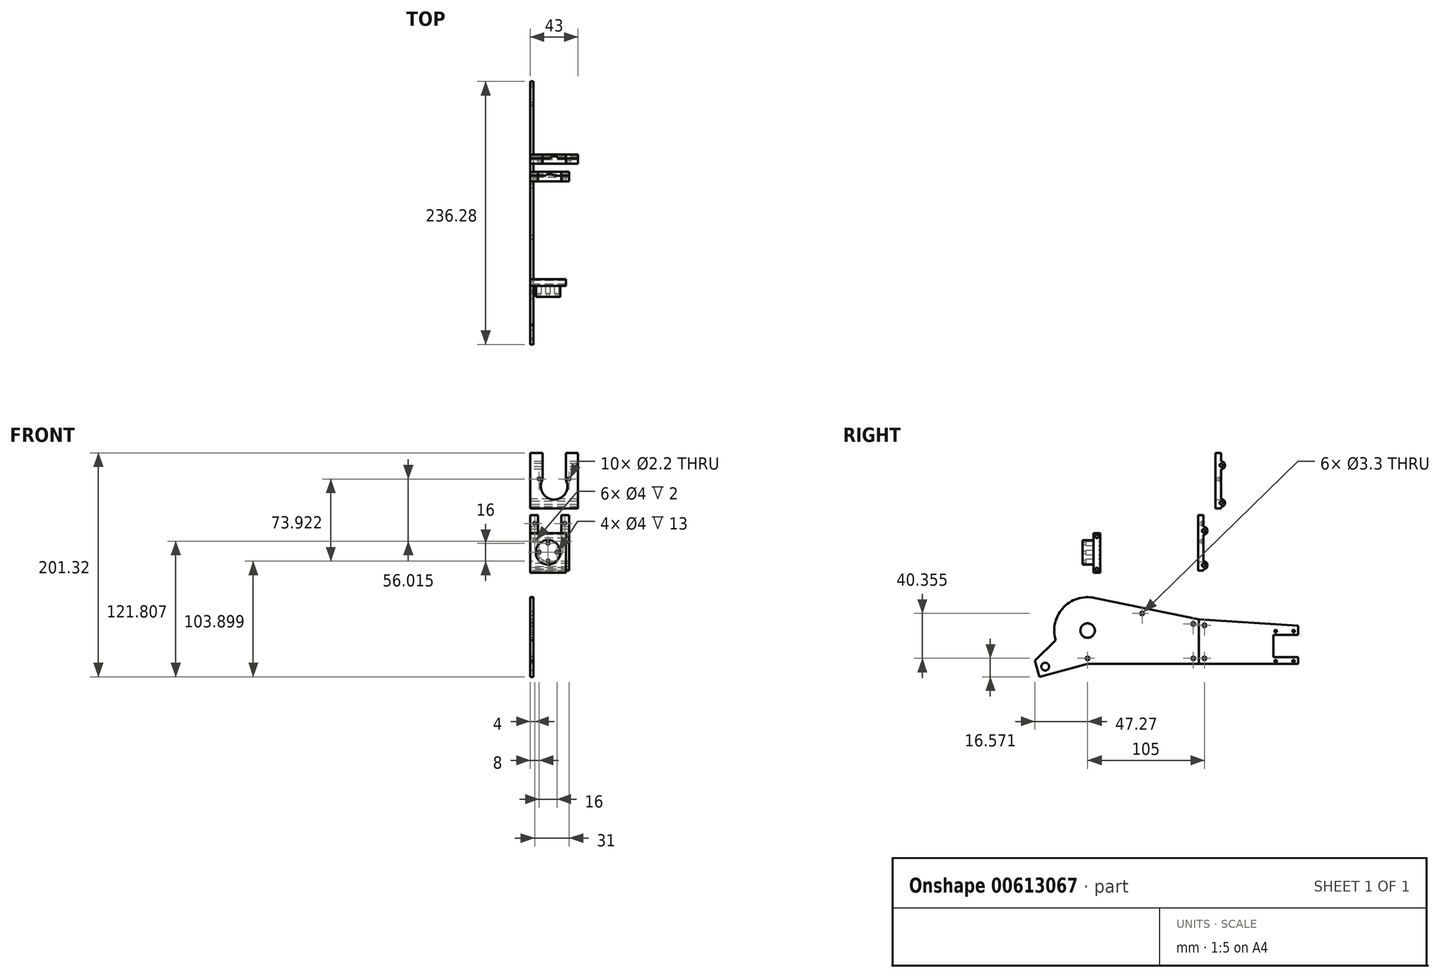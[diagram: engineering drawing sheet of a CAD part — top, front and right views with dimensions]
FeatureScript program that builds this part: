
annotation { "Feature Type Name" : "Feature", "Feature Type Description" : "" }
export const myFeature = defineFeature(function(context is Context, id is Id, definition is map)
    precondition{}
    {
        {
            var Q0;
            Q0=qCreatedBy(makeId("Right.planeOp"),FACE);
            var sketch = newSketch(context, id + "F0", { "sketchPlane" : qUnion([Q0])});
            skLineSegment(sketch, "E0", {"start": v(45.86, -61.42) * mm, "end": v(45.86, -101.42) * mm});
            skLineSegment(sketch, "E1", {"start": v(45.86, -101.42) * mm, "end": v(134.87, -101.42) * mm});
            skLineSegment(sketch, "E2", {"start": v(134.87, -101.42) * mm, "end": v(134.87, -95.42) * mm});
            skLineSegment(sketch, "E3", {"start": v(134.87, -66.9) * mm, "end": v(45.86, -61.42) * mm});
            skLineSegment(sketch, "E4", {"start": v(134.87, -95.42) * mm, "end": v(112.87, -95.42) * mm});
            skLineSegment(sketch, "E5", {"start": v(112.87, -95.42) * mm, "end": v(112.87, -75.42) * mm});
            skLineSegment(sketch, "E6", {"start": v(112.87, -75.42) * mm, "end": v(134.87, -75.42) * mm});
            skLineSegment(sketch, "E7.trimOffspring", {"start": v(134.87, -75.42) * mm, "end": v(134.87, -66.9) * mm});
            skPoint(sketch, "E8", {"position": v(50.86, -66.74) * mm});
            skPoint(sketch, "E9", {"position": v(50.86, -96.42) * mm});
            skCircle(sketch, "E10", {"center": v(145.37, -85.42) * mm, "radius": 11 * mm, "construction": true});
            skPoint(sketch, "E11", {"position": v(130.87, -98.92) * mm});
            skPoint(sketch, "E12", {"position": v(114.87, -98.92) * mm});
            skPoint(sketch, "E13", {"position": v(114.87, -71.92) * mm});
            skPoint(sketch, "E14", {"position": v(130.96, -71.92) * mm});
            skLineSegment(sketch, "E15", {"start": v(145.37, -85.42) * mm, "end": v(112.87, -85.42) * mm, "construction": true});
            skCircle(sketch, "E16", {"center": v(50.86, -66.74) * mm, "radius": 1.65 * mm});
            skCircle(sketch, "E17", {"center": v(50.86, -96.42) * mm, "radius": 1.65 * mm});
            skCircle(sketch, "E18", {"center": v(114.87, -71.92) * mm, "radius": 1.1 * mm});
            skCircle(sketch, "E19", {"center": v(130.96, -71.92) * mm, "radius": 1.1 * mm});
            skCircle(sketch, "E20", {"center": v(130.87, -98.92) * mm, "radius": 1.1 * mm});
            skCircle(sketch, "E21", {"center": v(114.87, -98.92) * mm, "radius": 1.1 * mm});
            skSolve(sketch);
        }
        {
            var Q0;
            Q0=makeQuery(id+"F0.imprint","IMPRINT",FACE,{"disambiguationData":[TD([[makeQuery(id+"F0.imprint","IMPRINT",EDGE,{"derivedFrom":sQuery(id+"F0.wireOp",EDGE,"E0")}),1.0]])]});
            extrude(context, id + "F1", {"entities" : qUnion([Q0]), "depth" : 3 * mm, "offsetDistance" : 25 * mm});
        }
        {
            var Q0;
            Q0=qCreatedBy(makeId("Right.planeOp"),FACE);
            var sketch = newSketch(context, id + "F2", { "sketchPlane" : qUnion([Q0])});
            skLineSegment(sketch, "E22", {"start": v(45.86, -61.42) * mm, "end": v(45.86, -101.42) * mm});
            skLineSegment(sketch, "E23", {"start": v(45.86, -101.42) * mm, "end": v(-54.14, -101.42) * mm});
            skArc(sketch, "E24", {"start": v(-54.14, -101.42) * mm, "mid": v(-83.82, -67.06) * mm, "end": v(-45.52, -42.68) * mm, "construction": true});
            skLineSegment(sketch, "E25", {"start": v(45.86, -61.42) * mm, "end": v(-45.52, -42.68) * mm});
            skCircle(sketch, "E26", {"center": v(-54.14, -71.42) * mm, "radius": 6.5 * mm});
            skLineSegment(sketch, "E27", {"start": v(-97.53, -113) * mm, "end": v(-101.41, -98.5) * mm});
            skLineSegment(sketch, "E28", {"start": v(-101.41, -98.5) * mm, "end": v(-82.9, -79.98) * mm});
            skCircle(sketch, "E29", {"center": v(-92.23, -103.81) * mm, "radius": 3.5 * mm});
            skLineSegment(sketch, "E30", {"start": v(-54.14, -71.42) * mm, "end": v(-92.23, -103.81) * mm, "construction": true});
            skLineSegment(sketch, "E31", {"start": v(-97.53, -113) * mm, "end": v(-54.14, -101.42) * mm});
            skPoint(sketch, "E32", {"position": v(40.86, -65.5) * mm});
            skPoint(sketch, "E33", {"position": v(40.86, -96.42) * mm});
            skLineSegment(sketch, "E34", {"start": v(-54.14, -71.42) * mm, "end": v(-54.14, -101.42) * mm, "construction": true});
            skPoint(sketch, "E35", {"position": v(-54.14, -96.42) * mm});
            skLineSegment(sketch, "E36", {"start": v(-54.14, -71.42) * mm, "end": v(-15.15, -48.9) * mm, "construction": true});
            skPoint(sketch, "E37", {"position": v(-5.15, -56.06) * mm});
            skCircle(sketch, "E38", {"center": v(-5.15, -56.06) * mm, "radius": 1.65 * mm});
            skCircle(sketch, "E39", {"center": v(40.86, -65.5) * mm, "radius": 1.65 * mm});
            skCircle(sketch, "E40", {"center": v(40.86, -96.42) * mm, "radius": 1.65 * mm});
            skCircle(sketch, "E41", {"center": v(-54.14, -96.42) * mm, "radius": 1.65 * mm});
            skArc(sketch, "E42", {"start": v(-45.52, -42.68) * mm, "mid": v(-75.33, -50.19) * mm, "end": v(-82.9, -79.98) * mm});
            skSolve(sketch);
        }
        {
            var Q0;
            {var subQ7=sQuery(id+"F2.wireOp",EDGE,"E22");Q0=makeQuery(id+"F2.imprint","IMPRINT",FACE,{"disambiguationData":[TD([[makeQuery(id+"F2.imprint","IMPRINT",EDGE,{"derivedFrom":subQ7}),-1.0]])]});}
            var Q1;
            {var subQ6=sQuery(id+"F2.wireOp",EDGE,"E24");var subQ9=makeQuery(id+"F2.imprint","INTERSECT",VERTEX,{"derivedFrom":[subQ6,sQuery(id+"F2.wireOp",EDGE,"E28")]});Q1=makeQuery(id+"F2.imprint","IMPRINT",FACE,{"disambiguationData":[TD([[makeQuery(id+"F2.imprint","IMPRINT",EDGE,{"disambiguationData":[TD([[subQ9,1.0]])],"derivedFrom":subQ6}),-1.0]])]});}
            var Q2;
            Q2=makeQuery(id+"F2.imprint","IMPRINT",FACE,{"disambiguationData":[TD([[makeQuery(id+"F2.imprint","IMPRINT",EDGE,{"derivedFrom":sQuery(id+"F2.wireOp",EDGE,"E27")}),-1.0]])]});
            extrude(context, id + "F3", {"entities" : qUnion([Q0, Q1, Q2]), "depth" : 3 * mm, "offsetDistance" : 25 * mm});
        }
        {
            var Q0;
            Q0=qCreatedBy(makeId("Right.planeOp"),FACE);
            var sketch = newSketch(context, id + "F4", { "sketchPlane" : qUnion([Q0])});
            skLineSegment(sketch, "E43", {"start": v(50.1, 32.32) * mm, "end": v(50.1, -17.68) * mm});
            skLineSegment(sketch, "E44", {"start": v(50.1, -17.68) * mm, "end": v(45.1, -17.68) * mm});
            skLineSegment(sketch, "E45", {"start": v(45.1, -17.68) * mm, "end": v(45.1, 32.32) * mm});
            skLineSegment(sketch, "E46", {"start": v(45.1, 32.32) * mm, "end": v(50.1, 32.32) * mm});
            skCircle(sketch, "E47", {"center": v(50.1, -12.68) * mm, "radius": 1.5 * mm});
            skCircle(sketch, "E48", {"center": v(50.1, -12.68) * mm, "radius": 3.5 * mm});
            skCircle(sketch, "E49", {"center": v(50.1, 18.24) * mm, "radius": 1.5 * mm});
            skCircle(sketch, "E50", {"center": v(50.1, 18.24) * mm, "radius": 3.5 * mm});
            skSolve(sketch);
        }
        {
            var Q0;
            Q0=qSketchRegion(id+"F4",true);
            extrude(context, id + "F5", {"entities" : qUnion([Q0]), "depth" : 35 * mm, "offsetDistance" : 25 * mm});
        }
        {
            var Q0;
            {var subQ0=sQuery(id+"F4.wireOp",EDGE,"E43");Q0=makeQuery(id+"F5.opExtrude","SWEPT_FACE",FACE,{"disambiguationData":[OSD([subQ0]),TDD([makeQuery(id+"F4.imprint","IMPRINT",EDGE,{"disambiguationData":[TD([[makeQuery(id+"F4.imprint","INTERSECT",VERTEX,{"derivedFrom":[subQ0,sQuery(id+"F4.wireOp",EDGE,"E46")]}),-1.0]])],"derivedFrom":subQ0})])]});}
            var sketch = newSketch(context, id + "F6", { "sketchPlane" : qUnion([Q0])});
            skCircle(sketch, "E51", {"center": v(-17.5, 2.32) * mm, "radius": 12 * mm});
            skPoint(sketch, "E52", {"position": v(-4, 24.82) * mm});
            skPoint(sketch, "E53", {"position": v(-4, 8.82) * mm});
            skPoint(sketch, "E54", {"position": v(-31, 8.82) * mm});
            skPoint(sketch, "E55", {"position": v(-31, 24.82) * mm});
            skLineSegment(sketch, "E56", {"start": v(-7, 8.13) * mm, "end": v(-7, 32.32) * mm});
            skLineSegment(sketch, "E57", {"start": v(-28, 32.32) * mm, "end": v(-28, 8.13) * mm});
            skLineSegment(sketch, "E58", {"start": v(-17.5, 2.32) * mm, "end": v(-17.5, 32.32) * mm, "construction": true});
            skSolve(sketch);
        }
        {
            var Q0;
            Q0=sQuery(id+"F6.wireOp",VERTEX,"E52");
            var Q1;
            Q1=sQuery(id+"F6.wireOp",VERTEX,"E53");
            var Q2;
            Q2=sQuery(id+"F6.wireOp",VERTEX,"E55");
            var Q3;
            Q3=sQuery(id+"F6.wireOp",VERTEX,"E54");
            var Q4;
            Q4=makeQuery(id+"FsGmeQWHbg3FPz0_0.opExtrude","SWEPT_BODY",BODY,{"disambiguationData":[OSD([sQuery(id+"FrUOqRR2quuCKey_0.wireOp",EDGE,"gyZbDc0t-850H-gwzf-YuIU-PHWtBzP6e17o.bottom"),sQuery(id+"FrUOqRR2quuCKey_0.wireOp",EDGE,"gyZbDc0t-850H-gwzf-YuIU-PHWtBzP6e17o.top"),sQuery(id+"FrUOqRR2quuCKey_0.wireOp",EDGE,"gyZbDc0t-850H-gwzf-YuIU-PHWtBzP6e17o.left"),sQuery(id+"FrUOqRR2quuCKey_0.wireOp",EDGE,"gyZbDc0t-850H-gwzf-YuIU-PHWtBzP6e17o.right")])]});
            var Q5;
            Q5=makeQuery(id+"F5.opExtrude","SWEPT_BODY",BODY,{"disambiguationData":[OSD([sQuery(id+"F4.wireOp",EDGE,"E43"),sQuery(id+"F4.wireOp",EDGE,"E44"),sQuery(id+"F4.wireOp",EDGE,"E45"),sQuery(id+"F4.wireOp",EDGE,"E46"),sQuery(id+"F4.wireOp",EDGE,"E47"),sQuery(id+"F4.wireOp",EDGE,"E48"),sQuery(id+"F4.wireOp",EDGE,"E49"),sQuery(id+"F4.wireOp",EDGE,"E50")])]});
            hole(context, id + "F7", {"style" : HoleStyle.C_BORE, "endStyle" : HoleEndStyle.BLIND, "holeDiameter" : 2.2 * mm, "cBoreDiameter" : 4 * mm, "cBoreDepth" : 2 * mm, "holeDepth" : 12 * mm, "isTappedThrough" : true, "tappedDepth" : 12 * mm, "tapClearance" : 3, "locations" : qUnion([Q0, Q1, Q2, Q3]), "scope" : qUnion([Q4, Q5])});
        }
        {
            var Q0;
            Q0=qSketchRegion(id+"F6",true);
            var Q1;
            {var subQ0=sQuery(id+"F6.wireOp",EDGE,"E56");var subQ1=sQuery(id+"F6.wireOp",EDGE,"E51");var subQ2=makeQuery(id+"F6.imprint","INTERSECT",VERTEX,{"derivedFrom":[subQ1,subQ0]});Q1=makeQuery(id+"F6.imprint","IMPRINT",FACE,{"disambiguationData":[TD([[makeQuery(id+"F6.imprint","IMPRINT",EDGE,{"disambiguationData":[TD([[subQ2,-1.0]])],"derivedFrom":subQ1}),-1.0]])]});}
            var Q2;
            {var subQ0=sQuery(id+"F6.wireOp",EDGE,"E56");var subQ1=sQuery(id+"F4.wireOp",EDGE,"E43");var subQ2=makeQuery(id+"F5.opExtrude","SWEPT_EDGE",EDGE,{"disambiguationData":[OSD([subQ1,sQuery(id+"F4.wireOp",EDGE,"E46")])]});var subQ3=makeQuery(id+"F6.imprint","INTERSECT",VERTEX,{"derivedFrom":[subQ2,subQ0]});Q2=makeQuery(id+"F6.imprint","IMPRINT",FACE,{"disambiguationData":[TD([[makeQuery(id+"F6.imprint","IMPRINT",EDGE,{"disambiguationData":[TD([[subQ3,1.0]])],"derivedFrom":subQ0}),1.0]])]});}
            extrude(context, id + "F8", {"entities" : qUnion([Q0, Q1, Q2]), "operationType" : NewBodyOperationType.REMOVE, "oppositeDirection" : true, "depth" : 25 * mm, "offsetDistance" : 25 * mm, "hasSecondDirection" : true, "secondDirectionOppositeDirection" : false, "secondDirectionDepth" : 25 * mm});
        }
        {
            var Q0;
            Q0=qCreatedBy(makeId("Right.planeOp"),FACE);
            var sketch = newSketch(context, id + "F9", { "sketchPlane" : qUnion([Q0])});
            skLineSegment(sketch, "E59.bottom", {"start": v(-48.72, 16.24) * mm, "end": v(-42.72, 16.24) * mm});
            skLineSegment(sketch, "E59.top", {"start": v(-48.72, -19.3) * mm, "end": v(-42.72, -19.3) * mm});
            skLineSegment(sketch, "E59.left", {"start": v(-48.72, 16.24) * mm, "end": v(-48.72, -19.3) * mm});
            skLineSegment(sketch, "E59.right", {"start": v(-42.72, 16.24) * mm, "end": v(-42.72, -19.3) * mm});
            skPoint(sketch, "E60", {"position": v(-45.72, 13.24) * mm});
            skPoint(sketch, "E61", {"position": v(-45.72, -16.44) * mm});
            skSolve(sketch);
        }
        {
            var Q0;
            Q0=qSketchRegion(id+"F9",true);
            extrude(context, id + "F10", {"entities" : qUnion([Q0]), "depth" : 32 * mm, "offsetDistance" : 25 * mm});
        }
        {
            var Q0;
            Q0=sQuery(id+"F9.wireOp",VERTEX,"E60");
            var Q1;
            Q1=sQuery(id+"F9.wireOp",VERTEX,"E61");
            var Q2;
            Q2=makeQuery(id+"F10.opExtrude","SWEPT_BODY",BODY,{"disambiguationData":[OSD([sQuery(id+"F9.wireOp",EDGE,"E59.bottom"),sQuery(id+"F9.wireOp",EDGE,"E59.top"),sQuery(id+"F9.wireOp",EDGE,"E59.left"),sQuery(id+"F9.wireOp",EDGE,"E59.right")])]});
            hole(context, id + "F11", {"style" : HoleStyle.SIMPLE, "endStyle" : HoleEndStyle.THROUGH, "oppositeDirection" : true, "holeDiameter" : 3 * mm, "majorDiameter" : 5 * mm, "isTappedThrough" : true, "tappedDepth" : 12 * mm, "tapClearance" : 3, "locations" : qUnion([Q0, Q1]), "scope" : qUnion([Q2])});
        }
        {
            var Q0;
            Q0=makeQuery(id+"F10.opExtrude","SWEPT_FACE",FACE,{"disambiguationData":[OSD([sQuery(id+"F9.wireOp",EDGE,"E59.right")])]});
            var sketch = newSketch(context, id + "F12", { "sketchPlane" : qUnion([Q0])});
            skCircle(sketch, "E62", {"center": v(-16, -1.1) * mm, "radius": 8 * mm, "construction": true});
            skLineSegment(sketch, "E63", {"start": v(-16, 6.9) * mm, "end": v(-16, -9.1) * mm, "construction": true});
            skLineSegment(sketch, "E64", {"start": v(-8, -1.1) * mm, "end": v(-24, -1.1) * mm, "construction": true});
            skPoint(sketch, "E65", {"position": v(-24, -1.1) * mm});
            skPoint(sketch, "E66", {"position": v(-16, 6.9) * mm});
            skPoint(sketch, "E67", {"position": v(-8, -1.1) * mm});
            skPoint(sketch, "E68", {"position": v(-16, -9.1) * mm});
            skCircle(sketch, "E69", {"center": v(-16, -1.1) * mm, "radius": 11 * mm});
            skSolve(sketch);
        }
        {
            var Q0;
            Q0=qSketchRegion(id+"F12",true);
            extrude(context, id + "F13", {"entities" : qUnion([Q0]), "operationType" : NewBodyOperationType.ADD, "oppositeDirection" : true, "depth" : 16 * mm, "offsetDistance" : 25 * mm});
        }
        {
            var Q0;
            Q0=sQuery(id+"F12.wireOp",VERTEX,"E66");
            var Q1;
            Q1=sQuery(id+"F12.wireOp",VERTEX,"E67");
            var Q2;
            Q2=sQuery(id+"F12.wireOp",VERTEX,"E68");
            var Q3;
            Q3=sQuery(id+"F12.wireOp",VERTEX,"E65");
            var Q4;
            Q4=makeQuery(id+"F10.opExtrude","SWEPT_BODY",BODY,{"disambiguationData":[OSD([sQuery(id+"F9.wireOp",EDGE,"E59.bottom"),sQuery(id+"F9.wireOp",EDGE,"E59.top"),sQuery(id+"F9.wireOp",EDGE,"E59.left"),sQuery(id+"F9.wireOp",EDGE,"E59.right")])]});
            hole(context, id + "F14", {"style" : HoleStyle.C_BORE, "endStyle" : HoleEndStyle.THROUGH, "holeDiameter" : 2.2 * mm, "cBoreDiameter" : 4 * mm, "cBoreDepth" : 13 * mm, "majorDiameter" : 5 * mm, "isTappedThrough" : true, "tappedDepth" : 12 * mm, "tapClearance" : 3, "locations" : qUnion([Q0, Q1, Q2, Q3]), "scope" : qUnion([Q4])});
        }
        {
            var Q0;
            Q0=qCreatedBy(makeId("Right.planeOp"),FACE);
            var sketch = newSketch(context, id + "F15", { "sketchPlane" : qUnion([Q0])});
            skLineSegment(sketch, "E70", {"start": v(65.88, 88.33) * mm, "end": v(65.88, 38.33) * mm});
            skLineSegment(sketch, "E71", {"start": v(65.88, 38.33) * mm, "end": v(60.88, 38.33) * mm});
            skLineSegment(sketch, "E72", {"start": v(60.88, 38.33) * mm, "end": v(60.88, 88.33) * mm});
            skLineSegment(sketch, "E73", {"start": v(60.88, 88.33) * mm, "end": v(65.88, 88.33) * mm});
            skCircle(sketch, "E74", {"center": v(65.88, 43.33) * mm, "radius": 1.45 * mm});
            skCircle(sketch, "E75", {"center": v(65.88, 43.33) * mm, "radius": 3.5 * mm});
            skCircle(sketch, "E76", {"center": v(65.88, 77.13) * mm, "radius": 1.45 * mm});
            skCircle(sketch, "E77", {"center": v(65.88, 77.13) * mm, "radius": 3.5 * mm});
            skSolve(sketch);
        }
        {
            var Q0;
            Q0=qSketchRegion(id+"F15",true);
            extrude(context, id + "F16", {"entities" : qUnion([Q0]), "depth" : 43 * mm, "offsetDistance" : 25 * mm});
        }
        {
            var Q0;
            {var subQ0=sQuery(id+"F15.wireOp",EDGE,"E70");Q0=makeQuery(id+"F16.opExtrude","SWEPT_FACE",FACE,{"disambiguationData":[OSD([subQ0]),TDD([makeQuery(id+"F15.imprint","IMPRINT",EDGE,{"disambiguationData":[TD([[makeQuery(id+"F15.imprint","INTERSECT",VERTEX,{"derivedFrom":[subQ0,sQuery(id+"F15.wireOp",EDGE,"E73")]}),-1.0]])],"derivedFrom":subQ0})])]});}
            var sketch = newSketch(context, id + "F17", { "sketchPlane" : qUnion([Q0])});
            skLineSegment(sketch, "E78", {"start": v(-21.5, 80.63) * mm, "end": v(-21.5, 61.1) * mm, "construction": true});
            skCircle(sketch, "E79", {"center": v(-21.5, 58.33) * mm, "radius": 12 * mm});
            skPoint(sketch, "E80", {"position": v(-35, 80.83) * mm});
            skPoint(sketch, "E81", {"position": v(-8, 80.83) * mm});
            skPoint(sketch, "E82", {"position": v(-35, 64.83) * mm});
            skPoint(sketch, "E83", {"position": v(-8, 64.83) * mm});
            skLineSegment(sketch, "E84", {"start": v(-11, 88.33) * mm, "end": v(-11, 64.14) * mm});
            skLineSegment(sketch, "E85", {"start": v(-32, 88.33) * mm, "end": v(-32, 64.14) * mm});
            skSolve(sketch);
        }
        {
            var Q0;
            {var subQ0=sQuery(id+"F17.wireOp",EDGE,"E84");var subQ1=sQuery(id+"F15.wireOp",EDGE,"E70");var subQ2=makeQuery(id+"F16.opExtrude","SWEPT_EDGE",EDGE,{"disambiguationData":[OSD([subQ1,sQuery(id+"F15.wireOp",EDGE,"E73")])]});var subQ3=makeQuery(id+"F17.imprint","INTERSECT",VERTEX,{"derivedFrom":[subQ2,subQ0]});Q0=makeQuery(id+"F17.imprint","IMPRINT",FACE,{"disambiguationData":[TD([[makeQuery(id+"F17.imprint","IMPRINT",EDGE,{"disambiguationData":[TD([[subQ3,-1.0]])],"derivedFrom":subQ0}),-1.0]])]});}
            var Q1;
            {var subQ0=sQuery(id+"F17.wireOp",EDGE,"E79");var subQ1=makeQuery(id+"F17.imprint","INTERSECT",VERTEX,{"derivedFrom":[subQ0,sQuery(id+"F17.wireOp",EDGE,"E84")]});Q1=makeQuery(id+"F17.imprint","IMPRINT",FACE,{"disambiguationData":[TD([[makeQuery(id+"F17.imprint","IMPRINT",EDGE,{"disambiguationData":[TD([[subQ1,-1.0]])],"derivedFrom":subQ0}),1.0]])]});}
            var Q2;
            {var subQ0=sQuery(id+"F17.wireOp",EDGE,"E84");var subQ1=sQuery(id+"F17.wireOp",EDGE,"E79");var subQ2=makeQuery(id+"F17.imprint","INTERSECT",VERTEX,{"derivedFrom":[subQ1,subQ0]});Q2=makeQuery(id+"F17.imprint","IMPRINT",FACE,{"disambiguationData":[TD([[makeQuery(id+"F17.imprint","IMPRINT",EDGE,{"disambiguationData":[TD([[subQ2,-1.0]])],"derivedFrom":subQ1}),-1.0]])]});}
            extrude(context, id + "F18", {"entities" : qUnion([Q0, Q1, Q2]), "operationType" : NewBodyOperationType.REMOVE, "endBound" : BoundingType.SYMMETRIC, "oppositeDirection" : true, "depth" : 25 * mm, "offsetDistance" : 25 * mm});
        }
        {
            var Q0;
            Q0=sQuery(id+"F17.wireOp",VERTEX,"E82");
            var Q1;
            Q1=sQuery(id+"F17.wireOp",VERTEX,"E83");
            var Q2;
            Q2=makeQuery(id+"F16.opExtrude","SWEPT_BODY",BODY,{"disambiguationData":[OSD([sQuery(id+"F15.wireOp",EDGE,"E70"),sQuery(id+"F15.wireOp",EDGE,"E71"),sQuery(id+"F15.wireOp",EDGE,"E72"),sQuery(id+"F15.wireOp",EDGE,"E73"),sQuery(id+"F15.wireOp",EDGE,"E74"),sQuery(id+"F15.wireOp",EDGE,"E75"),sQuery(id+"F15.wireOp",EDGE,"E76"),sQuery(id+"F15.wireOp",EDGE,"E77")])]});
            hole(context, id + "F19", {"style" : HoleStyle.C_BORE, "endStyle" : HoleEndStyle.THROUGH, "holeDiameter" : 2.2 * mm, "cBoreDiameter" : 4 * mm, "cBoreDepth" : 2 * mm, "majorDiameter" : 5 * mm, "isTappedThrough" : true, "tappedDepth" : 12 * mm, "tapClearance" : 3, "locations" : qUnion([Q0, Q1]), "scope" : qUnion([Q2])});
        }
    });
